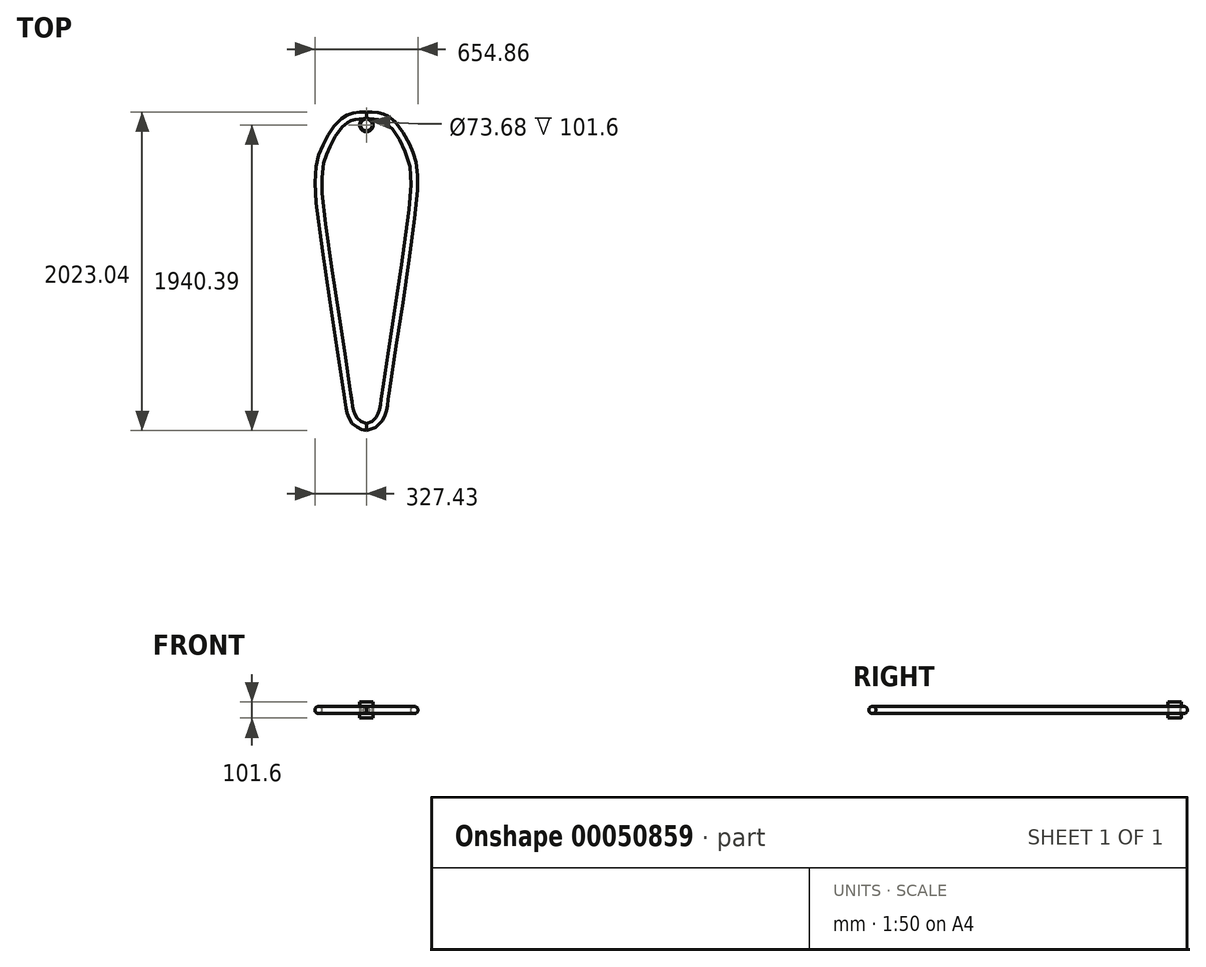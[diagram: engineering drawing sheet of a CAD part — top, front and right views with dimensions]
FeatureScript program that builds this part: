
annotation { "Feature Type Name" : "Feature", "Feature Type Description" : "" }
export const myFeature = defineFeature(function(context is Context, id is Id, definition is map)
    precondition{}
    {
        {
            var Q0;
            Q0=qCreatedBy(makeId("Top.planeOp"),FACE);
            var sketch = newSketch(context, id + "F0", { "sketchPlane" : qUnion([Q0])});
            skLineSegment(sketch, "E0.rect.bottom", {"start": v(304.8, 1000) * mm, "end": v(-304.8, 1000) * mm});
            skLineSegment(sketch, "E0.rect.top", {"start": v(304.8, -1000) * mm, "end": v(-304.8, -1000) * mm});
            skLineSegment(sketch, "E0.rect.left", {"start": v(304.8, 1000) * mm, "end": v(304.8, -1000) * mm});
            skLineSegment(sketch, "E0.rect.right", {"start": v(-304.8, 1000) * mm, "end": v(-304.8, -1000) * mm});
            skPoint(sketch, "E0.rect.middle", {"position": v(0, 0) * mm});
            skLineSegment(sketch, "E1", {"start": v(0, 934.96) * mm, "end": v(0, -864.09) * mm, "construction": true});
            skCircle(sketch, "E2", {"center": v(0, 934.96) * mm, "radius": 30.38 * mm});
            skPoint(sketch, "E3.endSnap0", {"position": v(0, 1000) * mm});
            skLineSegment(sketch, "E4", {"start": v(0, 1000) * mm, "end": v(0, 934.96) * mm, "construction": true});
            skPoint(sketch, "E5.2.internal.snap0", {"position": v(0, 967.48) * mm});
            skFitSpline(sketch, "E5", {"points": [v(0, 978.9) * mm, v(-68.73, 975.27) * mm, v(-101.86, 967.48) * mm, v(-154.7, 935.04) * mm, v(-225.7, 841.96) * mm, v(-289.6, 692.88) * mm, v(-304.8, 586.4) * mm, v(-289.47, 359.05) * mm, v(-124.94, -765.66) * mm, v(-110.97, -861.08) * mm, v(-101.5, -904.03) * mm, v(-85.87, -943.64) * mm, v(-62.44, -973.2) * mm, v(-21.16, -995.52) * mm, v(0, -1000) * mm], "startDerivative": vector(-1424.3, -8.15) * mm, "endDerivative": vector(497.85, -53.38) * mm});
            skLineSegment(sketch, "E6", {"start": v(0, -864.09) * mm, "end": v(0, -1019.2) * mm, "construction": true});
            skFitSpline(sketch, "E7.MirrorCS", {"points": [v(0, 978.9) * mm, v(68.73, 975.27) * mm, v(101.86, 967.48) * mm, v(154.7, 935.04) * mm, v(225.7, 841.96) * mm, v(289.6, 692.88) * mm, v(304.8, 586.4) * mm, v(289.47, 359.05) * mm, v(124.94, -765.66) * mm, v(110.97, -861.08) * mm, v(101.5, -904.03) * mm, v(85.87, -943.64) * mm, v(62.44, -973.2) * mm, v(21.16, -995.52) * mm, v(0, -1000) * mm], "startDerivative": vector(1424.3, -8.15) * mm, "endDerivative": vector(-497.85, -53.38) * mm});
            skSolve(sketch);
        }
        {
            var Q0;
            Q0=qCreatedBy(makeId("Right.planeOp"),FACE);
            var sketch = newSketch(context, id + "F1", { "sketchPlane" : qUnion([Q0])});
            skCircle(sketch, "E8", {"center": v(-1940.5, 0) * mm, "radius": 6.35 * mm});
            skCircle(sketch, "E9", {"center": v(-999.9, 0) * mm, "radius": 22.22 * mm});
            skSolve(sketch);
        }
        {
            var Q0;
            Q0=makeQuery(id+"F1.imprint","IMPRINT",FACE,{"disambiguationData":[TD([[makeQuery(id+"F1.imprint","IMPRINT",EDGE,{"derivedFrom":sQuery(id+"F1.wireOp",EDGE,"E9")}),1.0]])]});
            var Q1;
            Q1=sQuery(id+"F0.wireOp",EDGE,"E7.MirrorCS");
            var Q2;
            Q2=sQuery(id+"F0.wireOp",EDGE,"E5");
            sweep(context, id + "F2", {"profiles" : qUnion([Q0]), "path" : qUnion([Q1, Q2])});
        }
        {
            var Q0;
            Q0=qCreatedBy(makeId("Top.planeOp"),FACE);
            var sketch = newSketch(context, id + "F4", { "sketchPlane" : qUnion([Q0])});
            skCircle(sketch, "E10", {"center": v(0, 918.27) * mm, "radius": 36.84 * mm});
            skCircle(sketch, "E11", {"center": v(0, 918.27) * mm, "radius": 42.93 * mm});
            skSolve(sketch);
        }
        {
            var Q0;
            Q0 = qSketchRegion(id + "F4", true);
            var Q1;
            Q1=makeQuery(id+"F4.imprint","IMPRINT",FACE,{"disambiguationData":[TD([[makeQuery(id+"F4.imprint","IMPRINT",EDGE,{"derivedFrom":sQuery(id+"F4.wireOp",EDGE,"E10")}),-1.0]])]});
            extrude(context, id + "F3", {"entities" : qUnion([Q0, Q1]), "operationType" : NewBodyOperationType.ADD, "depth" : 50.8 * mm, "hasSecondDirection" : true, "secondDirectionOppositeDirection" : true, "secondDirectionDepth" : 50.8 * mm});
        }
    });
